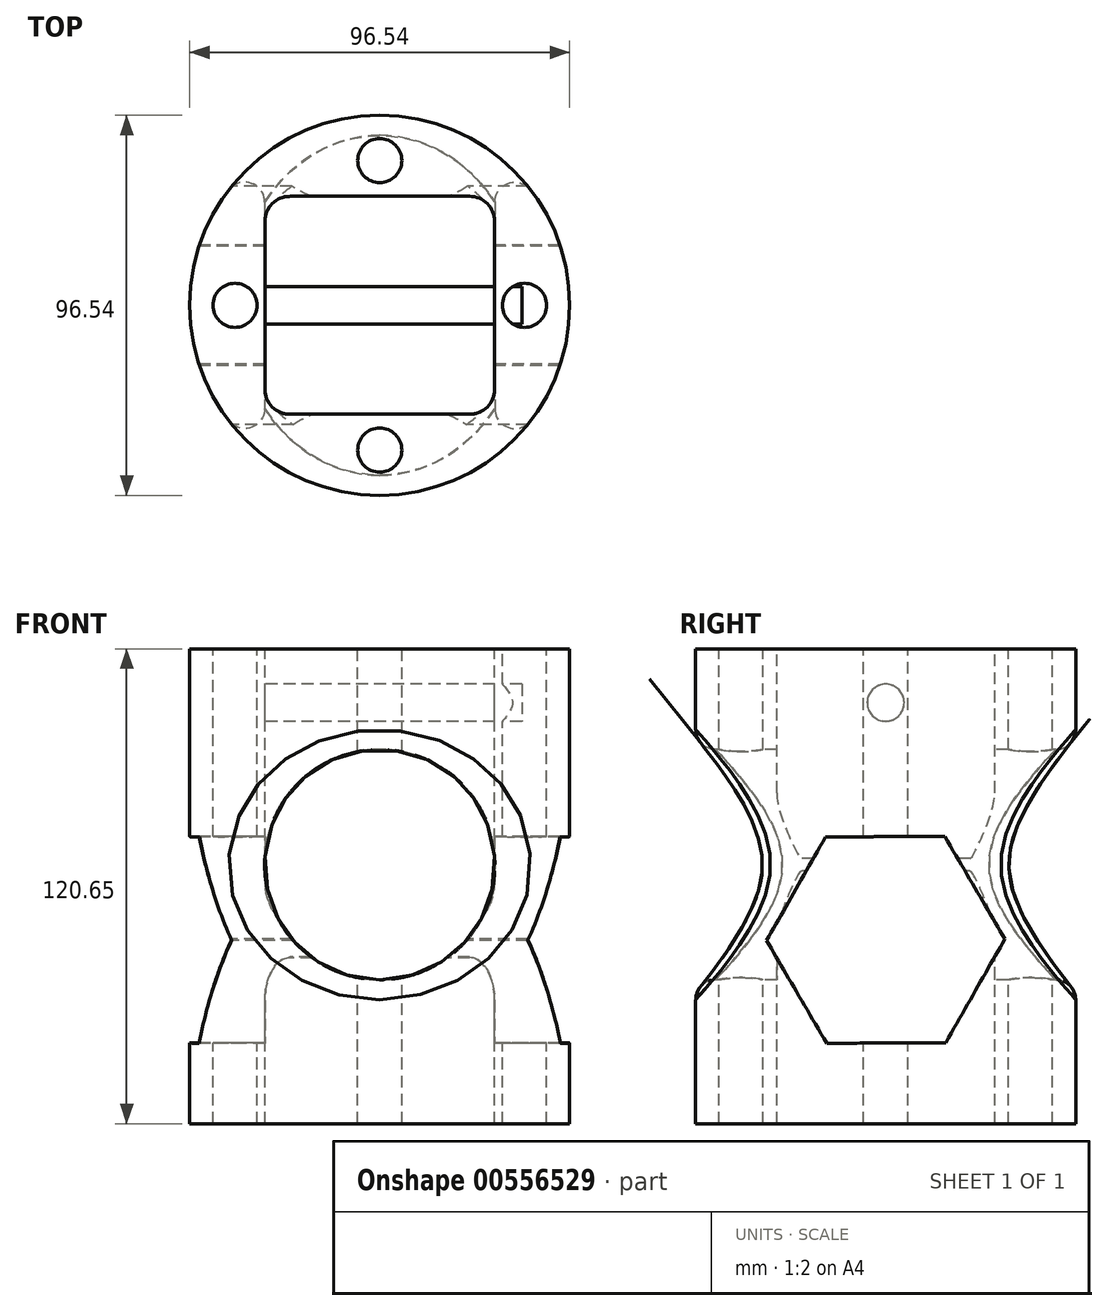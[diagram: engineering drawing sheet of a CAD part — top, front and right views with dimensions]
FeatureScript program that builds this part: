
annotation { "Feature Type Name" : "Feature", "Feature Type Description" : "" }
export const myFeature = defineFeature(function(context is Context, id is Id, definition is map)
    precondition{}
    {
        {
            var Q0;
            Q0=qCreatedBy(makeId("Top.planeOp"),FACE);
            var sketch = newSketch(context, id + "F0", { "sketchPlane" : qUnion([Q0])});
            skCircle(sketch, "E0", {"center": v(0, 0) * mm, "radius": 48.27 * mm});
            skSolve(sketch);
        }
        {
            var Q0;
            Q0=makeQuery(id+"F0.imprint","IMPRINT",FACE,{"disambiguationData":[TD([[makeQuery(id+"F0.imprint","IMPRINT",EDGE,{"derivedFrom":sQuery(id+"F0.wireOp",EDGE,"E0")}),1.0]])]});
            extrude(context, id + "F1", {"entities" : qUnion([Q0]), "depth" : 120.65 * mm, "offsetDistance" : 25.4 * mm});
        }
        {
            var Q0;
            Q0=makeQuery(id+"F1.opExtrude","CAP_FACE",FACE,{"disambiguationData":[OSD([sQuery(id+"F0.wireOp",EDGE,"E0")])],"isStart":false});
            var sketch = newSketch(context, id + "F2", { "sketchPlane" : qUnion([Q0])});
            skLineSegment(sketch, "E1.bottom", {"start": v(22.85, -27.68) * mm, "end": v(-22.85, -27.68) * mm});
            skLineSegment(sketch, "E1.top", {"start": v(22.85, 27.68) * mm, "end": v(-22.85, 27.68) * mm});
            skLineSegment(sketch, "E1.left", {"start": v(29.2, -21.33) * mm, "end": v(29.2, 21.33) * mm});
            skLineSegment(sketch, "E1.right", {"start": v(-29.2, -21.33) * mm, "end": v(-29.2, 21.33) * mm});
            skPoint(sketch, "E1.middle", {"position": v(0, 0) * mm});
            skPoint(sketch, "E2.visualSharp", {"position": v(-29.2, 27.68) * mm});
            skArc(sketch, "E2.filletArc", {"start": v(-22.85, 27.68) * mm, "mid": v(-27.34, 25.82) * mm, "end": v(-29.2, 21.33) * mm});
            skPoint(sketch, "E3.visualSharp", {"position": v(29.2, 27.68) * mm});
            skArc(sketch, "E3.filletArc", {"start": v(29.2, 21.33) * mm, "mid": v(27.34, 25.82) * mm, "end": v(22.85, 27.68) * mm});
            skPoint(sketch, "E4.visualSharp", {"position": v(29.2, -27.68) * mm});
            skArc(sketch, "E4.filletArc", {"start": v(22.85, -27.68) * mm, "mid": v(27.34, -25.82) * mm, "end": v(29.2, -21.33) * mm});
            skPoint(sketch, "E5.visualSharp", {"position": v(-29.2, -27.68) * mm});
            skArc(sketch, "E5.filletArc", {"start": v(-29.2, -21.33) * mm, "mid": v(-27.34, -25.82) * mm, "end": v(-22.85, -27.68) * mm});
            skSolve(sketch);
        }
        {
            var Q0;
            Q0=makeQuery(id+"F2.imprint","IMPRINT",FACE,{"disambiguationData":[TD([[makeQuery(id+"F2.imprint","IMPRINT",EDGE,{"derivedFrom":sQuery(id+"F2.wireOp",EDGE,"E1.bottom")}),-1.0]])]});
            extrude(context, id + "F3", {"entities" : qUnion([Q0]), "operationType" : NewBodyOperationType.REMOVE, "oppositeDirection" : true, "depth" : 170.43 * mm, "offsetDistance" : 25.4 * mm});
        }
        {
            var Q0;
            Q0=makeQuery(id+"F1.opExtrude","CAP_FACE",FACE,{"disambiguationData":[OSD([sQuery(id+"F0.wireOp",EDGE,"E0")])],"isStart":false});
            var sketch = newSketch(context, id + "F4", { "sketchPlane" : qUnion([Q0])});
            skCircle(sketch, "E6", {"center": v(0, 36.78) * mm, "radius": 5.6 * mm});
            skCircle(sketch, "E7.1.0", {"center": v(36.78, 0) * mm, "radius": 5.6 * mm});
            skCircle(sketch, "E7.2.0", {"center": v(0, -36.78) * mm, "radius": 5.6 * mm});
            skPoint(sketch, "E7.center", {"position": v(0, 0) * mm});
            skLineSegment(sketch, "E7.anchor1", {"start": v(0, 0) * mm, "end": v(0, 36.78) * mm, "construction": true});
            skLineSegment(sketch, "E7.anchor2", {"start": v(0, 0) * mm, "end": v(0, -36.78) * mm, "construction": true});
            skCircle(sketch, "E8.1.0", {"center": v(-36.78, 0) * mm, "radius": 5.6 * mm});
            skSolve(sketch);
        }
        {
            var Q0;
            Q0=makeQuery(id+"F4.imprint","IMPRINT",FACE,{"disambiguationData":[TD([[makeQuery(id+"F4.imprint","IMPRINT",EDGE,{"derivedFrom":sQuery(id+"F4.wireOp",EDGE,"E8.1.0")}),1.0]])]});
            var Q1;
            Q1=makeQuery(id+"F4.imprint","IMPRINT",FACE,{"disambiguationData":[TD([[makeQuery(id+"F4.imprint","IMPRINT",EDGE,{"derivedFrom":sQuery(id+"F4.wireOp",EDGE,"E6")}),1.0]])]});
            var Q2;
            Q2=makeQuery(id+"F4.imprint","IMPRINT",FACE,{"disambiguationData":[TD([[makeQuery(id+"F4.imprint","IMPRINT",EDGE,{"derivedFrom":sQuery(id+"F4.wireOp",EDGE,"E7.1.0")}),1.0]])]});
            var Q3;
            Q3=makeQuery(id+"F4.imprint","IMPRINT",FACE,{"disambiguationData":[TD([[makeQuery(id+"F4.imprint","IMPRINT",EDGE,{"derivedFrom":sQuery(id+"F4.wireOp",EDGE,"E7.2.0")}),1.0]])]});
            extrude(context, id + "F5", {"entities" : qUnion([Q0, Q1, Q2, Q3]), "operationType" : NewBodyOperationType.REMOVE, "oppositeDirection" : true, "depth" : 180.34 * mm, "offsetDistance" : 25.4 * mm});
        }
        {
            var Q0;
            Q0=qCreatedBy(makeId("Front.planeOp"),FACE);
            var sketch = newSketch(context, id + "F6", { "sketchPlane" : qUnion([Q0])});
            skCircle(sketch, "E9", {"center": v(0, 65.82) * mm, "radius": 29.24 * mm});
            skSolve(sketch);
        }
        {
            var Q0;
            Q0=makeQuery(id+"F6.imprint","IMPRINT",FACE,{"disambiguationData":[TD([[makeQuery(id+"F6.imprint","IMPRINT",EDGE,{"derivedFrom":sQuery(id+"F6.wireOp",EDGE,"E9")}),1.0]])]});
            extrude(context, id + "F7", {"entities" : qUnion([Q0]), "operationType" : NewBodyOperationType.REMOVE, "oppositeDirection" : true, "depth" : 197.1 * mm, "offsetDistance" : 25.4 * mm, "hasSecondDirection" : true, "secondDirectionOppositeDirection" : false, "secondDirectionDepth" : 185.42 * mm});
        }
        {
            var Q0;
            Q0=makeQuery(id+"F7.boolean.opBoolean","INTERSECT",EDGE,{"disambiguationData":[OD(1.0)],"derivedFrom":[makeQuery(id+"F1.opExtrude","SWEPT_FACE",FACE,{"disambiguationData":[OSD([sQuery(id+"F0.wireOp",EDGE,"E0")])]}),makeQuery(id+"F7.opExtrude","SWEPT_FACE",FACE,{"disambiguationData":[OSD([sQuery(id+"F6.wireOp",EDGE,"E9")])]})]});
            fillet(context, id + "F8", {"entities" : qUnion([Q0]), "radius" : 5.08 * mm, "tangentPropagation" : true, "allowEdgeOverflow" : false});
        }
        {
            var Q0;
            Q0=makeQuery(id+"F7.boolean.opBoolean","INTERSECT",EDGE,{"disambiguationData":[OD(0.0)],"derivedFrom":[makeQuery(id+"F1.opExtrude","SWEPT_FACE",FACE,{"disambiguationData":[OSD([sQuery(id+"F0.wireOp",EDGE,"E0")])]}),makeQuery(id+"F7.opExtrude","SWEPT_FACE",FACE,{"disambiguationData":[OSD([sQuery(id+"F6.wireOp",EDGE,"E9")])]})]});
            fillet(context, id + "F9", {"entities" : qUnion([Q0]), "radius" : 5.08 * mm, "tangentPropagation" : true, "allowEdgeOverflow" : false});
        }
        {
            var Q0;
            Q0=qCreatedBy(makeId("Right.planeOp"),FACE);
            var sketch = newSketch(context, id + "F10", { "sketchPlane" : qUnion([Q0])});
            skCircle(sketch, "E10.cCircle", {"center": v(0, 46.71) * mm, "radius": 26.21 * mm, "construction": true});
            skLineSegment(sketch, "E10.0", {"start": v(30.27, 46.88) * mm, "end": v(15.28, 20.59) * mm});
            skLineSegment(sketch, "E10.1", {"start": v(15.28, 20.59) * mm, "end": v(-14.99, 20.42) * mm});
            skLineSegment(sketch, "E10.2", {"start": v(-14.99, 20.42) * mm, "end": v(-30.27, 46.54) * mm});
            skLineSegment(sketch, "E10.3", {"start": v(-30.27, 46.54) * mm, "end": v(-15.28, 72.84) * mm});
            skLineSegment(sketch, "E10.4", {"start": v(-15.28, 72.84) * mm, "end": v(14.99, 73.01) * mm});
            skLineSegment(sketch, "E10.5", {"start": v(14.99, 73.01) * mm, "end": v(30.27, 46.88) * mm});
            skPoint(sketch, "E10.0.midPoint", {"position": v(22.78, 33.74) * mm});
            skSolve(sketch);
        }
        {
            var Q0;
            Q0=makeQuery(id+"F10.imprint","IMPRINT",FACE,{"disambiguationData":[TD([[makeQuery(id+"F10.imprint","IMPRINT",EDGE,{"derivedFrom":sQuery(id+"F10.wireOp",EDGE,"E10.0")}),-1.0]])]});
            extrude(context, id + "F11", {"entities" : qUnion([Q0]), "operationType" : NewBodyOperationType.REMOVE, "depth" : 148.34 * mm, "offsetDistance" : 25.4 * mm, "hasSecondDirection" : true, "secondDirectionOppositeDirection" : true, "secondDirectionDepth" : 123.44 * mm});
        }
        {
            var Q0;
            Q0=makeQuery(id+"F7.boolean.opBoolean","SPLIT",FACE,{"disambiguationData":[TD([makeQuery(id+"F1.opExtrude","CAP_FACE",FACE,{"disambiguationData":[OSD([sQuery(id+"F0.wireOp",EDGE,"E0")])],"isStart":false})])],"derivedFrom":makeQuery(id+"F3.boolean.opBoolean","COPY",FACE,{"derivedFrom":makeQuery(id+"F3.opExtrude","SWEPT_FACE",FACE,{"disambiguationData":[OSD([sQuery(id+"F2.wireOp",EDGE,"E1.right")])]})})});
            var sketch = newSketch(context, id + "F12", { "sketchPlane" : qUnion([Q0])});
            skCircle(sketch, "E11", {"center": v(0, 106.96) * mm, "radius": 4.71 * mm});
            skSolve(sketch);
        }
        {
            var Q0;
            Q0=makeQuery(id+"F12.imprint","IMPRINT",FACE,{"disambiguationData":[TD([[makeQuery(id+"F12.imprint","IMPRINT",EDGE,{"derivedFrom":sQuery(id+"F12.wireOp",EDGE,"E11")}),1.0]])]});
            extrude(context, id + "F13", {"entities" : qUnion([Q0]), "operationType" : NewBodyOperationType.ADD, "depth" : 65.28 * mm, "offsetDistance" : 25.4 * mm});
        }
    });
